SOLIDWORKS PART (.sldprt)
format: sldprt  version: not decoded by parser v0  size: 253,952 bytes
history: native  units: mm
features: sketch x4, extrude x2, fillet x2, material x1, surface_op x1, shell x1, cut_extrude x1 (+13 scaffold rows collapsed)
feature tree (25):
  scaffold x13  (default folders/planes/origin — collapsed)
  material  "Material <not specified>"
  sketch  "Sketch1"  dims[D1=6.0mm]
  extrude  "Boss-Extrude1"  Depth=4mm
  fillet  "Fillet1"  Radius=6mm
  sketch  "Sketch2"  dims[D1=2.0mm]
  surface_op  "Surface-Extrude1"
  shell  "Shell1"  Thickness=1mm
  sketch  "Sketch4"  dims[c1.D2=~13.321753mm c1.D3=~12.983065mm c2.D2=~14.62006mm c2.D3=~16.313503mm c3.D2=~14.281371mm c3.D3=~13.321753mm c4.D2=~13.660442mm c4.D3=~15.093686mm c5.D2=4.0mm c5.D3=4.0mm c5.D4=4.0mm c5.D5=4.0mm c5.D6=4.0mm c5.D7=4.0mm c5.D8=~15.093686mm c5.D9=4.0mm c6.D8=4.0mm c6.D1=0.0mm]
  extrude  "Boss-Extrude3"  Depth=0.2mm
  fillet  "Fillet2"  Radius=2mm
  sketch  "Sketch6"  dims[D1=1.0mm]
  cut_extrude  "Cut-Extrude1"  [1 undecoded]
decode coverage: 9 of 11 modeling features carry decoded parameters
note: ~ marks probable driven/reference dimensions
note: 1 parameter value undecoded
note: suppression state not decoded; provenance and decode notes live in map.json
